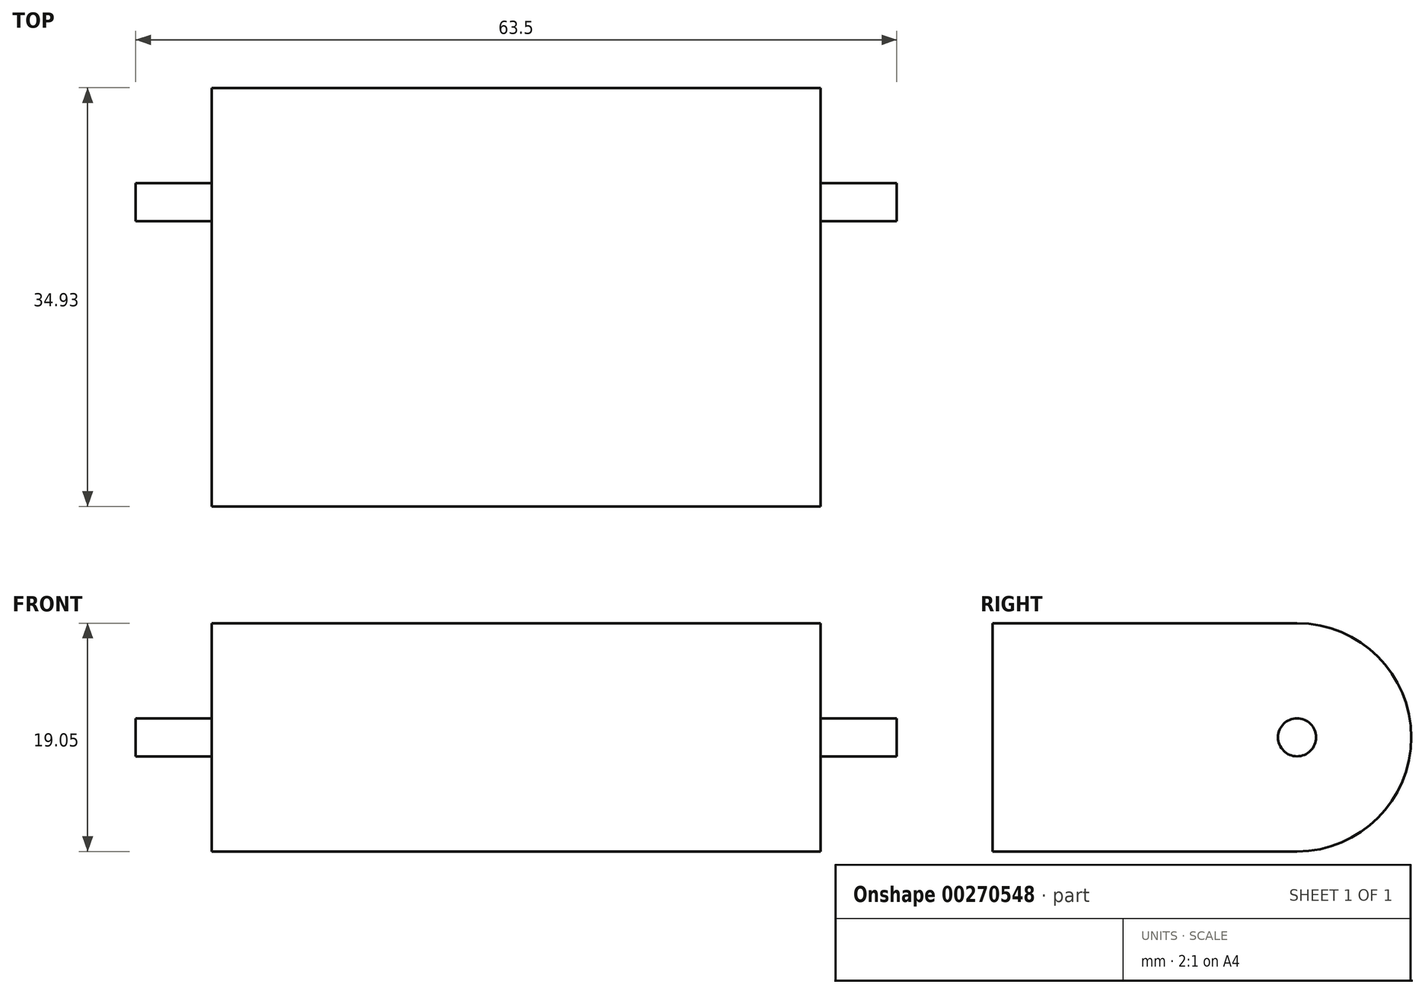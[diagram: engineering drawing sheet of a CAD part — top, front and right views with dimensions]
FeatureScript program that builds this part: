
annotation { "Feature Type Name" : "Feature", "Feature Type Description" : "" }
export const myFeature = defineFeature(function(context is Context, id is Id, definition is map)
    precondition{}
    {
        {
            var Q0;
            Q0=qCreatedBy(makeId("Right.planeOp"),FACE);
            var sketch = newSketch(context, id + "F0", { "sketchPlane" : qUnion([Q0])});
            skLineSegment(sketch, "E0.bottom", {"start": v(0, 19.05) * mm, "end": v(-25.4, 19.05) * mm});
            skLineSegment(sketch, "E0.top", {"start": v(0, 0) * mm, "end": v(-25.4, 0) * mm});
            skLineSegment(sketch, "E0.left", {"start": v(0, 19.05) * mm, "end": v(0, 0) * mm});
            skLineSegment(sketch, "E0.right", {"start": v(-25.4, 19.05) * mm, "end": v(-25.4, 0) * mm});
            skArc(sketch, "E1", {"start": v(0, 0) * mm, "mid": v(9.53, 9.53) * mm, "end": v(0, 19.05) * mm});
            skSolve(sketch);
        }
        {
            var Q0;
            Q0=makeQuery(id+"F0.imprint","IMPRINT",FACE,{"disambiguationData":[TD([[makeQuery(id+"F0.imprint","IMPRINT",EDGE,{"derivedFrom":sQuery(id+"F0.wireOp",EDGE,"E0.bottom")}),1.0]])]});
            var Q1;
            Q1=makeQuery(id+"F0.imprint","IMPRINT",FACE,{"disambiguationData":[TD([[makeQuery(id+"F0.imprint","IMPRINT",EDGE,{"derivedFrom":sQuery(id+"F0.wireOp",EDGE,"E0.left")}),1.0]])]});
            extrude(context, id + "F1", {"entities" : qUnion([Q0, Q1]), "depth" : 50.8 * mm});
        }
        {
            var Q0;
            Q0=makeQuery(id+"F1.opExtrude","CAP_FACE",FACE,{"disambiguationData":[OSD([sQuery(id+"F0.wireOp",EDGE,"E0.bottom"),sQuery(id+"F0.wireOp",EDGE,"E0.top"),sQuery(id+"F0.wireOp",EDGE,"E0.right"),sQuery(id+"F0.wireOp",EDGE,"E1")])],"isStart":false});
            var sketch = newSketch(context, id + "F2", { "sketchPlane" : qUnion([Q0])});
            skCircle(sketch, "E2", {"center": v(0, 9.53) * mm, "radius": 1.59 * mm});
            skSolve(sketch);
        }
        {
            var Q0;
            Q0=makeQuery(id+"F1.opExtrude","CAP_FACE",FACE,{"disambiguationData":[OSD([sQuery(id+"F0.wireOp",EDGE,"E0.bottom"),sQuery(id+"F0.wireOp",EDGE,"E0.top"),sQuery(id+"F0.wireOp",EDGE,"E0.right"),sQuery(id+"F0.wireOp",EDGE,"E1")])],"isStart":true});
            var sketch = newSketch(context, id + "F3", { "sketchPlane" : qUnion([Q0])});
            skCircle(sketch, "E3", {"center": v(0, 9.53) * mm, "radius": 1.59 * mm});
            skSolve(sketch);
        }
        {
            var Q0;
            Q0=makeQuery(id+"F2.imprint","IMPRINT",FACE,{"disambiguationData":[TD([[makeQuery(id+"F2.imprint","IMPRINT",EDGE,{"derivedFrom":sQuery(id+"F2.wireOp",EDGE,"E2")}),1.0]])]});
            var Q1;
            Q1=sQuery(id+"F2.wireOp",EDGE,"E2");
            extrude(context, id + "F4", {"entities" : qUnion([Q0]), "operationType" : NewBodyOperationType.ADD, "surfaceEntities" : qUnion([Q1]), "depth" : 6.35 * mm});
        }
        {
            var Q0;
            Q0=makeQuery(id+"F3.imprint","IMPRINT",FACE,{"disambiguationData":[TD([[makeQuery(id+"F3.imprint","IMPRINT",EDGE,{"derivedFrom":sQuery(id+"F3.wireOp",EDGE,"E3")}),1.0]])]});
            var Q1;
            Q1=sQuery(id+"F3.wireOp",EDGE,"E3");
            extrude(context, id + "F5", {"entities" : qUnion([Q0]), "operationType" : NewBodyOperationType.ADD, "surfaceEntities" : qUnion([Q1]), "depth" : 6.35 * mm});
        }
    });
